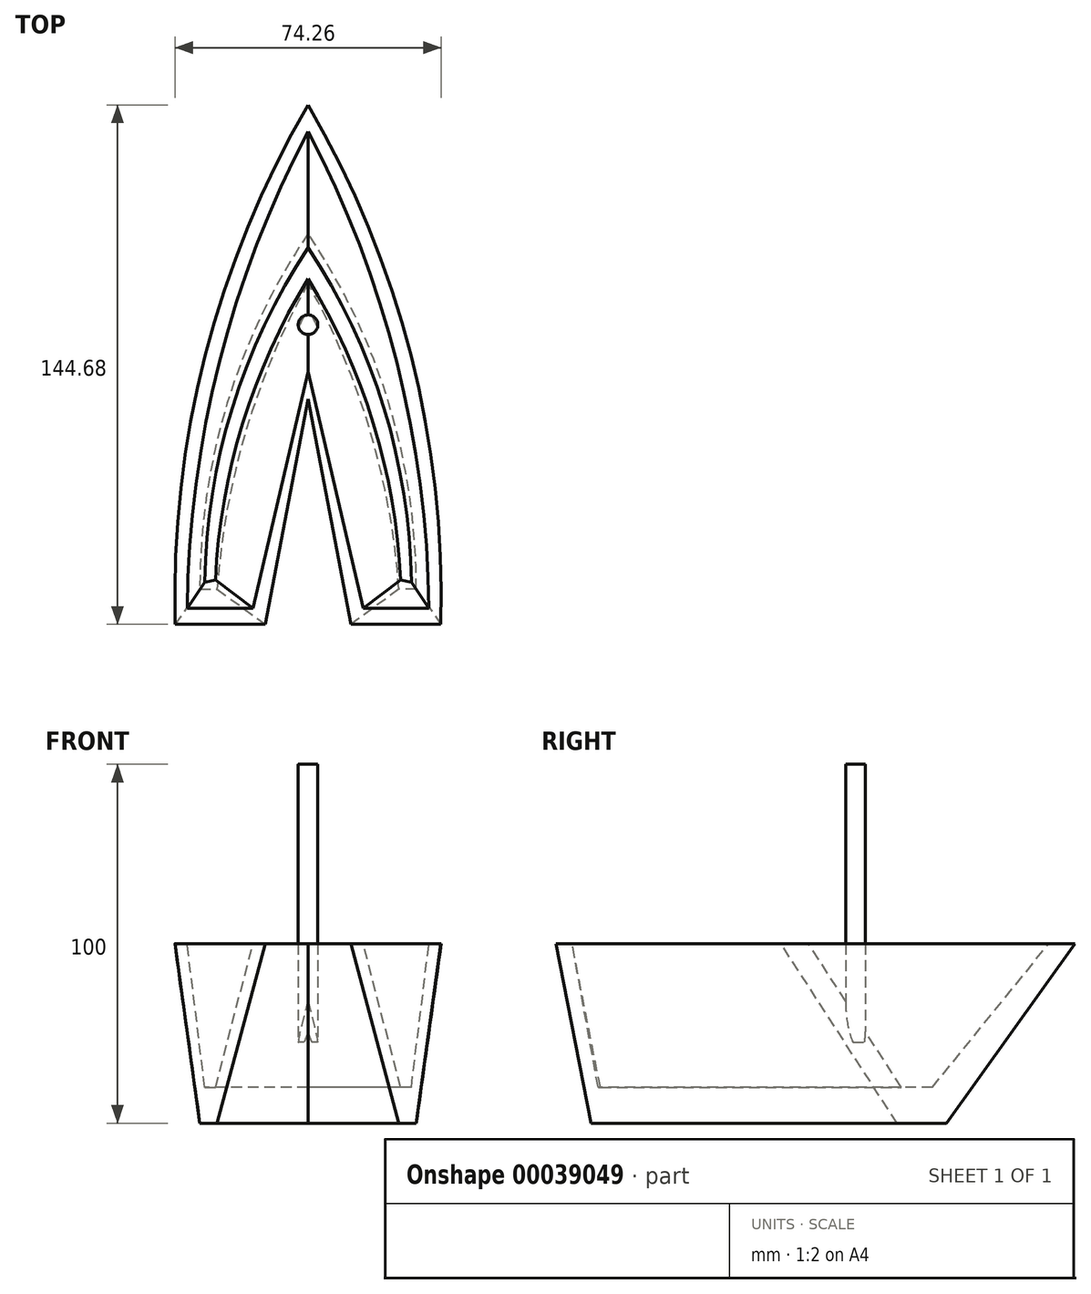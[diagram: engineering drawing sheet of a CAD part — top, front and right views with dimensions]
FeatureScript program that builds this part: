
annotation { "Feature Type Name" : "Feature", "Feature Type Description" : "" }
export const myFeature = defineFeature(function(context is Context, id is Id, definition is map)
    precondition{}
    {
        {
            var Q0;
            Q0=qCreatedBy(makeId("Top.planeOp"),FACE);
            var sketch = newSketch(context, id + "F0", { "sketchPlane" : qUnion([Q0])});
            skArc(sketch, "E0", {"start": v(37.02, -95.04) * mm, "mid": v(28.66, -20.1) * mm, "end": v(0, 49.64) * mm});
            skLineSegment(sketch, "E1", {"start": v(37.02, -95.04) * mm, "end": v(11.94, -95.04) * mm});
            skLineSegment(sketch, "E2", {"start": v(0, -32.35) * mm, "end": v(11.94, -95.04) * mm});
            skArc(sketch, "E3.MirrorCS", {"start": v(-37.02, -95.04) * mm, "mid": v(-28.66, -20.1) * mm, "end": v(0, 49.64) * mm});
            skLineSegment(sketch, "E4.MirrorCS", {"start": v(0, -32.35) * mm, "end": v(-11.94, -95.04) * mm});
            skLineSegment(sketch, "E5.MirrorCS", {"start": v(-37.02, -95.04) * mm, "end": v(-11.94, -95.04) * mm});
            skSolve(sketch);
        }
        {
            var Q0;
            Q0=qCreatedBy(makeId("Top.planeOp"),FACE);
            cPlane(context, id + "F1", {"entities" : qUnion([Q0]), "cplaneType" : CPlaneType.OFFSET, "offset" : 50 * mm, "oppositeDirection" : true, "width" : 152.4 * mm, "height" : 152.4 * mm});
        }
        {
            var Q0;
            Q0=qCreatedBy(id+"F1.planeOp",FACE);
            var sketch = newSketch(context, id + "F2", { "sketchPlane" : qUnion([Q0])});
            skArc(sketch, "E6", {"start": v(0, 13.8) * mm, "mid": v(-22.53, -33.46) * mm, "end": v(-30.18, -85.27) * mm});
            skLineSegment(sketch, "E7", {"start": v(-30.18, -85.27) * mm, "end": v(-25.34, -85.27) * mm});
            skArc(sketch, "E8", {"start": v(0, 0) * mm, "mid": v(-17.33, -41.25) * mm, "end": v(-25.34, -85.27) * mm});
            skArc(sketch, "E9.MirrorCS", {"start": v(0, 13.8) * mm, "mid": v(22.53, -33.46) * mm, "end": v(30.18, -85.27) * mm});
            skArc(sketch, "E10.MirrorCS", {"start": v(0, 0) * mm, "mid": v(17.33, -41.25) * mm, "end": v(25.34, -85.27) * mm});
            skLineSegment(sketch, "E11.MirrorCS", {"start": v(30.18, -85.27) * mm, "end": v(25.34, -85.27) * mm});
            skSolve(sketch);
        }
        {
            var Q0;
            Q0=makeQuery(id+"F2.imprint","IMPRINT",FACE,{"disambiguationData":[TD([[makeQuery(id+"F2.imprint","IMPRINT",EDGE,{"derivedFrom":sQuery(id+"F2.wireOp",EDGE,"E6")}),1.0]])]});
            var Q1;
            Q1=makeQuery(id+"F0.imprint","IMPRINT",FACE,{"disambiguationData":[TD([[makeQuery(id+"F0.imprint","IMPRINT",EDGE,{"derivedFrom":sQuery(id+"F0.wireOp",EDGE,"E0")}),1.0]])]});
            loft(context, id + "F3", {"sheetProfilesArray" : [{ "sheetProfileEntities" : qUnion([Q0]) }, { "sheetProfileEntities" : qUnion([Q1]) }]});
        }
        {
            var Q0;
            Q0=qCreatedBy(makeId("Top.planeOp"),FACE);
            var sketch = newSketch(context, id + "F4", { "sketchPlane" : qUnion([Q0])});
            skArc(sketch, "E12", {"start": v(33.7, -90.57) * mm, "mid": v(24.75, -22.13) * mm, "end": v(0, 42.3) * mm});
            skLineSegment(sketch, "E13", {"start": v(33.7, -90.57) * mm, "end": v(15.36, -90.57) * mm});
            skLineSegment(sketch, "E14", {"start": v(15.36, -90.57) * mm, "end": v(0, -24.67) * mm});
            skLineSegment(sketch, "E15.MirrorCS", {"start": v(-15.36, -90.57) * mm, "end": v(0, -24.67) * mm});
            skLineSegment(sketch, "E16.MirrorCS", {"start": v(-33.7, -90.57) * mm, "end": v(-15.36, -90.57) * mm});
            skArc(sketch, "E17.MirrorCS", {"start": v(-33.7, -90.57) * mm, "mid": v(-24.75, -22.13) * mm, "end": v(0, 42.3) * mm});
            skSolve(sketch);
        }
        {
            var Q0;
            Q0=qCreatedBy(makeId("Top.planeOp"),FACE);
            cPlane(context, id + "F5", {"entities" : qUnion([Q0]), "cplaneType" : CPlaneType.OFFSET, "offset" : 40 * mm, "oppositeDirection" : true, "width" : 150 * mm, "height" : 150 * mm});
        }
        {
            var Q0;
            Q0=qCreatedBy(id+"F5.planeOp",FACE);
            var sketch = newSketch(context, id + "F6", { "sketchPlane" : qUnion([Q0])});
            skArc(sketch, "E18", {"start": v(0, 9.88) * mm, "mid": v(-21.1, -34.65) * mm, "end": v(-28.8, -83.32) * mm});
            skArc(sketch, "E19", {"start": v(0.21, 1.57) * mm, "mid": v(-18.16, -38.9) * mm, "end": v(-25.8, -82.68) * mm});
            skLineSegment(sketch, "E20", {"start": v(-28.8, -83.32) * mm, "end": v(-25.8, -82.68) * mm});
            skArc(sketch, "E21.MirrorCS", {"start": v(-0.21, 1.57) * mm, "mid": v(18.16, -38.9) * mm, "end": v(25.8, -82.68) * mm});
            skArc(sketch, "E22.MirrorCS", {"start": v(0, 9.88) * mm, "mid": v(21.1, -34.65) * mm, "end": v(28.8, -83.32) * mm});
            skLineSegment(sketch, "E23.MirrorCS", {"start": v(28.8, -83.32) * mm, "end": v(25.8, -82.68) * mm});
            skSolve(sketch);
        }
        {
            var Q1;
            Q1 = qSketchRegion(id + "F6", true);
            var Q2;
            Q2 = qSketchRegion(id + "F4", true);
            loft(context, id + "F7", {"operationType" : NewBodyOperationType.REMOVE, "sheetProfilesArray" : [{ "sheetProfileEntities" : qUnion([Q1]) }, { "sheetProfileEntities" : qUnion([Q2]) }]});
        }
        {
            var Q0;
            Q0=qCreatedBy(makeId("Top.planeOp"),FACE);
            cPlane(context, id + "F8", {"entities" : qUnion([Q0]), "cplaneType" : CPlaneType.OFFSET, "offset" : 25 * mm, "oppositeDirection" : true, "width" : 150 * mm, "height" : 150 * mm});
        }
        {
            var Q0;
            Q0=qCreatedBy(id+"F8.planeOp",FACE);
            var sketch = newSketch(context, id + "F9", { "sketchPlane" : qUnion([Q0])});
            skCircle(sketch, "E24", {"center": v(0, -11.58) * mm, "radius": 2.74 * mm});
            skSolve(sketch);
        }
        {
            var Q0;
            Q0 = qSketchRegion(id + "F9", true);
            extrude(context, id + "F10", {"entities" : qUnion([Q0]), "operationType" : NewBodyOperationType.ADD, "depth" : 75 * mm});
        }
        {
            var Q0;
            Q0 = qSketchRegion(id + "F9", true);
            extrude(context, id + "F11", {"entities" : qUnion([Q0]), "operationType" : NewBodyOperationType.ADD, "oppositeDirection" : true, "depth" : 2.5 * mm});
        }
    });
